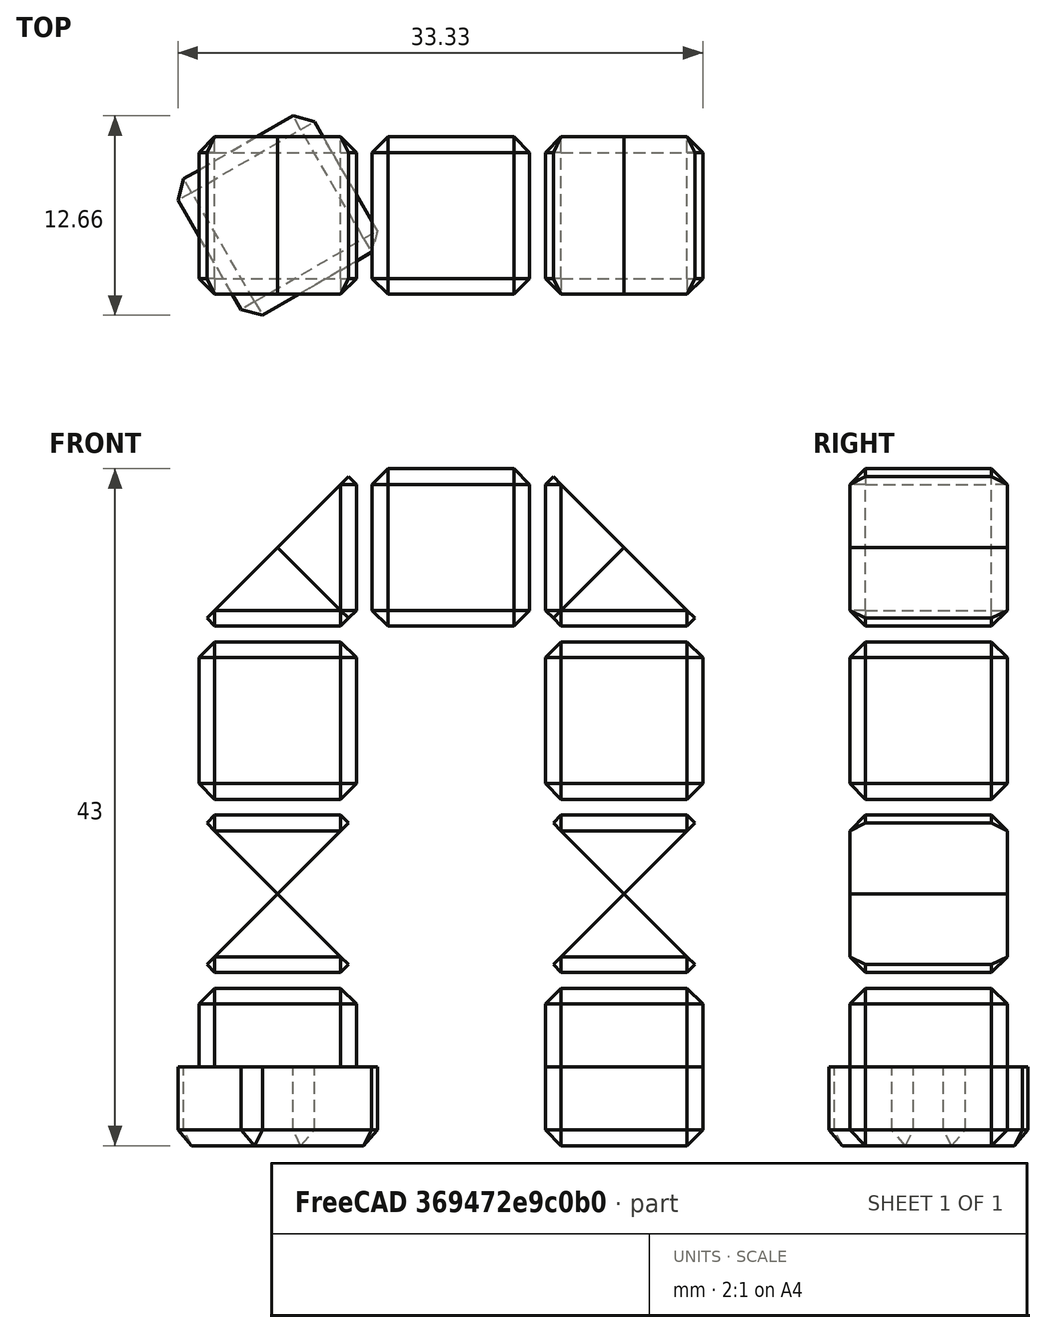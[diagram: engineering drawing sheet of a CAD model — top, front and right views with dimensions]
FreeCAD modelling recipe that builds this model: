
FCSTD DOCUMENT  (FreeCAD 0.18.4R)
Label: robot-layout
License: All rights reserved
LicenseURL: http://en.wikipedia.org/wiki/All_rights_reserved
objects: Part::Box×43, Part::Chamfer×15, Part::Cut×14, Part::Mirroring×9, Part::Fuse×8, Part::MultiCommon×6
note: 95 computed .brp shape members not serialized (recipe doc carries the construction recipe); baked Part::Feature solids carry a one-line shape summary decoded from their .brp

FEATURE [Part::Box] Box  label="Cube"
  AttacherType = Attacher::AttachEngine3D
  Height = 10
  Length = 10
  Width = 10
FEATURE [Part::Chamfer] Chamfer
  Base = -> Box
  Edges = 12 edges r=1: [Edge1,Edge2,Edge3,Edge4,Edge5,Edge6,Edge7,Edge8,Edge9,Edge10,Edge11,Edge12]
FEATURE [Part::Box] Box001  label="Cube001"
  AttacherType = Attacher::AttachEngine3D
  Height = 10
  Length = 10
  Width = 10
FEATURE [Part::Chamfer] Chamfer001
  Base = -> Box001
  Edges = 12 edges r=1: [Edge1,Edge2,Edge3,Edge4,Edge5,Edge6,Edge7,Edge8,Edge9,Edge10,Edge11,Edge12]
  Placement = pos=(0,0,11) rot=(0,0,1;0rad)
FEATURE [Part::Box] Box002  label="Cube002"
  AttacherType = Attacher::AttachEngine3D
  Height = 10
  Length = 10
  Width = 10
FEATURE [Part::Chamfer] Chamfer002
  Base = -> Box002
  Edges = 12 edges r=1: [Edge1,Edge2,Edge3,Edge4,Edge5,Edge6,Edge7,Edge8,Edge9,Edge10,Edge11,Edge12]
  Placement = pos=(0,0,22) rot=(0,0,1;0rad)
FEATURE [Part::Box] Box004  label="Cube004"
  AttacherType = Attacher::AttachEngine3D
  Height = 10
  Length = 10
  Width = 10
FEATURE [Part::Chamfer] Chamfer004
  Base = -> Box004
  Edges = 12 edges r=1: [Edge1,Edge2,Edge3,Edge4,Edge5,Edge6,Edge7,Edge8,Edge9,Edge10,Edge11,Edge12]
  Placement = pos=(11,0,33) rot=(0,0,1;0rad)
FEATURE [Part::Box] Box006  label="Cube006"
  AttacherType = Attacher::AttachEngine3D
  Height = 10
  Length = 10
  Width = 10
FEATURE [Part::Chamfer] Chamfer006
  Base = -> Box006
  Edges = 12 edges r=1: [Edge1,Edge2,Edge3,Edge4,Edge5,Edge6,Edge7,Edge8,Edge9,Edge10,Edge11,Edge12]
  Placement = pos=(22,0,22) rot=(0,0,1;0rad)
FEATURE [Part::Box] Box009  label="Cube009"
  AttacherType = Attacher::AttachEngine3D
  Height = 10
  Length = 15
  Placement = pos=(-2,-2,-5) rot=(0,0,1;0rad)
  Width = 16
FEATURE [Part::Box] Box010  label="Cube010"
  AttacherType = Attacher::AttachEngine3D
  Height = 10
  Length = 10
  Width = 10
FEATURE [Part::Chamfer] Chamfer009
  Base = -> Box010
  Edges = 12 edges r=1: [Edge1,Edge2,Edge3,Edge4,Edge5,Edge6,Edge7,Edge8,Edge9,Edge10,Edge11,Edge12]
FEATURE [Part::Box] Box011  label="Cube011"
  AttacherType = Attacher::AttachEngine3D
  Height = 10
  Length = 15
  Placement = pos=(-2,-2,-5) rot=(0,0,1;0rad)
  Width = 16
FEATURE [Part::MultiCommon] Common
  Placement = pos=(3.16987,-1.83013,0) rot=(0,0,1;0.523599rad)
  Shapes = -> [Box011,Chamfer009]
FEATURE [Part::Cut] Cut
  Base = -> Chamfer
  Tool = -> Box009
FEATURE [Part::Box] Box012  label="Cube012"
  AttacherType = Attacher::AttachEngine3D
  Height = 10
  Length = 10
  Width = 10
FEATURE [Part::Chamfer] Chamfer010
  Base = -> Box012
  Edges = 12 edges r=1: [Edge1,Edge2,Edge3,Edge4,Edge5,Edge6,Edge7,Edge8,Edge9,Edge10,Edge11,Edge12]
FEATURE [Part::Box] Box013  label="Cube013"
  AttacherType = Attacher::AttachEngine3D
  Height = 10
  Length = 15
  Placement = pos=(-2,-2,-5) rot=(0,0,1;0rad)
  Width = 16
FEATURE [Part::Box] Box014  label="Cube014"
  AttacherType = Attacher::AttachEngine3D
  Height = 10
  Length = 15
  Placement = pos=(-2,-2,-5) rot=(0,0,1;0rad)
  Width = 16
FEATURE [Part::Box] Box015  label="Cube015"
  AttacherType = Attacher::AttachEngine3D
  Height = 10
  Length = 10
  Width = 10
FEATURE [Part::Chamfer] Chamfer011
  Base = -> Box015
  Edges = 12 edges r=1: [Edge1,Edge2,Edge3,Edge4,Edge5,Edge6,Edge7,Edge8,Edge9,Edge10,Edge11,Edge12]
FEATURE [Part::MultiCommon] Common001
  Placement = pos=(22,0,0) rot=(0,0,1;0rad)
  Shapes = -> [Box014,Chamfer011]
FEATURE [Part::Cut] Cut001
  Base = -> Chamfer010
  Placement = pos=(22,0,0) rot=(0,0,1;0rad)
  Tool = -> Box013
FEATURE [Part::Box] Box016  label="Cube016"
  AttacherType = Attacher::AttachEngine3D
  Height = 10
  Length = 10
  Placement = pos=(5,-5,16) rot=(0,1,0;0.785398rad)
  Width = 21
FEATURE [Part::Box] Box017  label="Cube017"
  AttacherType = Attacher::AttachEngine3D
  Height = 10
  Length = 10
  Placement = pos=(5,-5,16) rot=(0,1,0;0.785398rad)
  Width = 21
FEATURE [Part::Mirroring] Part__Mirroring  label="Cube017 (Mirror #1)"
  Base = (0,0,0)
  Normal = (1,0,0)
  Placement = pos=(10,0,0) rot=(0,0,1;0rad)
  Source = -> Box017
FEATURE [Part::Fuse] Fusion
  Base = -> Box016
  Tool = -> Part__Mirroring
FEATURE [Part::Box] Box019  label="Cube019"
  AttacherType = Attacher::AttachEngine3D
  Height = 10
  Length = 10
  Placement = pos=(5,-5,16) rot=(0,1,0;0.785398rad)
  Width = 21
FEATURE [Part::Box] Box020  label="Cube020"
  AttacherType = Attacher::AttachEngine3D
  Height = 10
  Length = 10
  Placement = pos=(5,-5,16) rot=(0,1,0;0.785398rad)
  Width = 21
FEATURE [Part::Mirroring] Part__Mirroring001  label="Cube017 (Mirror #1)001"
  Base = (0,0,0)
  Normal = (1,0,0)
  Placement = pos=(10,0,0) rot=(0,0,1;0rad)
  Source = -> Box020
FEATURE [Part::Fuse] Fusion001
  Base = -> Box019
  Tool = -> Part__Mirroring001
FEATURE [Part::Box] Box021  label="Cube021"
  AttacherType = Attacher::AttachEngine3D
  Height = 10
  Length = 10
  Width = 10
FEATURE [Part::Chamfer] Chamfer012
  Base = -> Box021
  Edges = 12 edges r=1: [Edge1,Edge2,Edge3,Edge4,Edge5,Edge6,Edge7,Edge8,Edge9,Edge10,Edge11,Edge12]
  Placement = pos=(0,0,11) rot=(0,0,1;0rad)
FEATURE [Part::Box] Box022  label="Cube022"
  AttacherType = Attacher::AttachEngine3D
  Height = 10
  Length = 15
  Placement = pos=(-2,-2,6) rot=(0,0,1;0rad)
  Width = 16
FEATURE [Part::Box] Box023  label="Cube023"
  AttacherType = Attacher::AttachEngine3D
  Height = 10
  Length = 15
  Placement = pos=(-2,-2,6) rot=(0,0,1;0rad)
  Width = 16
FEATURE [Part::Cut] Cut002
  Base = -> Chamfer001
  Tool = -> Box022
FEATURE [Part::MultiCommon] Common002
  Shapes = -> [Box023,Chamfer012]
FEATURE [Part::Cut] Cut003
  Base = -> Cut002
  Tool = -> Fusion001
FEATURE [Part::Cut] Cut004
  Base = -> Common002
  Tool = -> Fusion
FEATURE [Part::Box] Box024  label="Cube024"
  AttacherType = Attacher::AttachEngine3D
  Height = 10
  Length = 10
  Width = 10
FEATURE [Part::Chamfer] Chamfer013
  Base = -> Box024
  Edges = 12 edges r=1: [Edge1,Edge2,Edge3,Edge4,Edge5,Edge6,Edge7,Edge8,Edge9,Edge10,Edge11,Edge12]
  Placement = pos=(0,0,11) rot=(0,0,1;0rad)
FEATURE [Part::Box] Box025  label="Cube025"
  AttacherType = Attacher::AttachEngine3D
  Height = 10
  Length = 10
  Placement = pos=(5,-5,16) rot=(0,1,0;0.785398rad)
  Width = 21
FEATURE [Part::Box] Box026  label="Cube026"
  AttacherType = Attacher::AttachEngine3D
  Height = 10
  Length = 10
  Placement = pos=(5,-5,16) rot=(0,1,0;0.785398rad)
  Width = 21
FEATURE [Part::Mirroring] Part__Mirroring002  label="Cube017 (Mirror #1)002"
  Base = (0,0,0)
  Normal = (1,0,0)
  Placement = pos=(10,0,0) rot=(0,0,1;0rad)
  Source = -> Box026
FEATURE [Part::Fuse] Fusion002
  Base = -> Box025
  Tool = -> Part__Mirroring002
FEATURE [Part::Box] Box027  label="Cube027"
  AttacherType = Attacher::AttachEngine3D
  Height = 10
  Length = 15
  Placement = pos=(-2,-2,6) rot=(0,0,1;0rad)
  Width = 16
FEATURE [Part::Cut] Cut005
  Base = -> Chamfer013
  Tool = -> Box027
FEATURE [Part::Cut] Cut006
  Base = -> Cut005
  Placement = pos=(-11,0,43) rot=(0,1,0;1.5708rad)
  Tool = -> Fusion002
FEATURE [Part::Box] Box028  label="Cube028"
  AttacherType = Attacher::AttachEngine3D
  Height = 10
  Length = 10
  Placement = pos=(5,-5,16) rot=(0,1,0;0.785398rad)
  Width = 21
FEATURE [Part::Box] Box029  label="Cube029"
  AttacherType = Attacher::AttachEngine3D
  Height = 10
  Length = 10
  Placement = pos=(5,-5,16) rot=(0,1,0;0.785398rad)
  Width = 21
FEATURE [Part::Mirroring] Part__Mirroring003  label="Cube017 (Mirror #1)003"
  Base = (0,0,0)
  Normal = (1,0,0)
  Placement = pos=(10,0,0) rot=(0,0,1;0rad)
  Source = -> Box029
FEATURE [Part::Fuse] Fusion003
  Base = -> Box028
  Tool = -> Part__Mirroring003
FEATURE [Part::Box] Box030  label="Cube030"
  AttacherType = Attacher::AttachEngine3D
  Height = 10
  Length = 10
  Width = 10
FEATURE [Part::Chamfer] Chamfer014
  Base = -> Box030
  Edges = 12 edges r=1: [Edge1,Edge2,Edge3,Edge4,Edge5,Edge6,Edge7,Edge8,Edge9,Edge10,Edge11,Edge12]
  Placement = pos=(0,0,11) rot=(0,0,1;0rad)
FEATURE [Part::Box] Box031  label="Cube031"
  AttacherType = Attacher::AttachEngine3D
  Height = 10
  Length = 15
  Placement = pos=(-2,-2,6) rot=(0,0,1;0rad)
  Width = 16
FEATURE [Part::MultiCommon] Common003
  Shapes = -> [Box031,Chamfer014]
FEATURE [Part::Cut] Cut007
  Base = -> Common003
  Placement = pos=(0,0,22) rot=(0,0,1;0rad)
  Tool = -> Fusion003
FEATURE [Part::Box] Box032  label="Cube032"
  AttacherType = Attacher::AttachEngine3D
  Height = 10
  Length = 10
  Placement = pos=(5,-5,16) rot=(0,1,0;0.785398rad)
  Width = 21
FEATURE [Part::Box] Box033  label="Cube033"
  AttacherType = Attacher::AttachEngine3D
  Height = 10
  Length = 10
  Width = 10
FEATURE [Part::Box] Box034  label="Cube034"
  AttacherType = Attacher::AttachEngine3D
  Height = 10
  Length = 10
  Placement = pos=(5,-5,16) rot=(0,1,0;0.785398rad)
  Width = 21
FEATURE [Part::Chamfer] Chamfer015
  Base = -> Box033
  Edges = 12 edges r=1: [Edge1,Edge2,Edge3,Edge4,Edge5,Edge6,Edge7,Edge8,Edge9,Edge10,Edge11,Edge12]
  Placement = pos=(0,0,11) rot=(0,0,1;0rad)
FEATURE [Part::Mirroring] Part__Mirroring004  label="Cube017 (Mirror #1)004"
  Base = (0,0,0)
  Normal = (1,0,0)
  Placement = pos=(10,0,0) rot=(0,0,1;0rad)
  Source = -> Box034
FEATURE [Part::Fuse] Fusion004
  Base = -> Box032
  Tool = -> Part__Mirroring004
FEATURE [Part::Box] Box035  label="Cube035"
  AttacherType = Attacher::AttachEngine3D
  Height = 10
  Length = 15
  Placement = pos=(-2,-2,6) rot=(0,0,1;0rad)
  Width = 16
FEATURE [Part::Cut] Cut009
  Base = -> Chamfer015
  Tool = -> Box035
FEATURE [Part::Cut] Cut008
  Base = -> Cut009
  Placement = pos=(-11,0,43) rot=(0,1,0;1.5708rad)
  Tool = -> Fusion004
FEATURE [Part::Mirroring] Part__Mirroring005  label="Cut008 (Mirror #6)"
  Base = (-5,0,0)
  Normal = (1,0,0)
  Placement = pos=(42,0,0) rot=(0,0,1;0rad)
  Source = -> Cut008
FEATURE [Part::Box] Box036  label="Cube036"
  AttacherType = Attacher::AttachEngine3D
  Height = 10
  Length = 10
  Placement = pos=(5,-5,16) rot=(0,1,0;0.785398rad)
  Width = 21
FEATURE [Part::Box] Box037  label="Cube037"
  AttacherType = Attacher::AttachEngine3D
  Height = 10
  Length = 15
  Placement = pos=(-2,-2,6) rot=(0,0,1;0rad)
  Width = 16
FEATURE [Part::Box] Box038  label="Cube038"
  AttacherType = Attacher::AttachEngine3D
  Height = 10
  Length = 10
  Placement = pos=(5,-5,16) rot=(0,1,0;0.785398rad)
  Width = 21
FEATURE [Part::Mirroring] Part__Mirroring006  label="Cube017 (Mirror #1)005"
  Base = (0,0,0)
  Normal = (1,0,0)
  Placement = pos=(10,0,0) rot=(0,0,1;0rad)
  Source = -> Box038
FEATURE [Part::Box] Box039  label="Cube039"
  AttacherType = Attacher::AttachEngine3D
  Height = 10
  Length = 10
  Width = 10
FEATURE [Part::Chamfer] Chamfer016
  Base = -> Box039
  Edges = 12 edges r=1: [Edge1,Edge2,Edge3,Edge4,Edge5,Edge6,Edge7,Edge8,Edge9,Edge10,Edge11,Edge12]
  Placement = pos=(0,0,11) rot=(0,0,1;0rad)
FEATURE [Part::MultiCommon] Common004
  Shapes = -> [Box037,Chamfer016]
FEATURE [Part::Fuse] Fusion005
  Base = -> Box036
  Tool = -> Part__Mirroring006
FEATURE [Part::Cut] Cut010
  Base = -> Common004
  Placement = pos=(22,0,22) rot=(0,0,1;0rad)
  Tool = -> Fusion005
FEATURE [Part::Box] Box040  label="Cube040"
  AttacherType = Attacher::AttachEngine3D
  Height = 10
  Length = 10
  Width = 10
FEATURE [Part::Chamfer] Chamfer017
  Base = -> Box040
  Edges = 12 edges r=1: [Edge1,Edge2,Edge3,Edge4,Edge5,Edge6,Edge7,Edge8,Edge9,Edge10,Edge11,Edge12]
  Placement = pos=(0,0,11) rot=(0,0,1;0rad)
FEATURE [Part::Box] Box041  label="Cube041"
  AttacherType = Attacher::AttachEngine3D
  Height = 10
  Length = 10
  Placement = pos=(5,-5,16) rot=(0,1,0;0.785398rad)
  Width = 21
FEATURE [Part::Box] Box042  label="Cube042"
  AttacherType = Attacher::AttachEngine3D
  Height = 10
  Length = 10
  Placement = pos=(5,-5,16) rot=(0,1,0;0.785398rad)
  Width = 21
FEATURE [Part::Mirroring] Part__Mirroring007  label="Cube017 (Mirror #1)006"
  Base = (0,0,0)
  Normal = (1,0,0)
  Placement = pos=(10,0,0) rot=(0,0,1;0rad)
  Source = -> Box042
FEATURE [Part::Fuse] Fusion006
  Base = -> Box041
  Tool = -> Part__Mirroring007
FEATURE [Part::Box] Box043  label="Cube043"
  AttacherType = Attacher::AttachEngine3D
  Height = 10
  Length = 15
  Placement = pos=(-2,-2,6) rot=(0,0,1;0rad)
  Width = 16
FEATURE [Part::Cut] Cut011
  Base = -> Chamfer017
  Tool = -> Box043
FEATURE [Part::Cut] Cut012
  Base = -> Cut011
  Placement = pos=(22,0,0) rot=(0,0,1;0rad)
  Tool = -> Fusion006
FEATURE [Part::Box] Box044  label="Cube044"
  AttacherType = Attacher::AttachEngine3D
  Height = 10
  Length = 10
  Placement = pos=(5,-5,16) rot=(0,1,0;0.785398rad)
  Width = 21
FEATURE [Part::Box] Box045  label="Cube045"
  AttacherType = Attacher::AttachEngine3D
  Height = 10
  Length = 10
  Placement = pos=(5,-5,16) rot=(0,1,0;0.785398rad)
  Width = 21
FEATURE [Part::Mirroring] Part__Mirroring008  label="Cube017 (Mirror #1)007"
  Base = (0,0,0)
  Normal = (1,0,0)
  Placement = pos=(10,0,0) rot=(0,0,1;0rad)
  Source = -> Box045
FEATURE [Part::Fuse] Fusion007
  Base = -> Box044
  Tool = -> Part__Mirroring008
FEATURE [Part::Box] Box046  label="Cube046"
  AttacherType = Attacher::AttachEngine3D
  Height = 10
  Length = 10
  Width = 10
FEATURE [Part::Chamfer] Chamfer018
  Base = -> Box046
  Edges = 12 edges r=1: [Edge1,Edge2,Edge3,Edge4,Edge5,Edge6,Edge7,Edge8,Edge9,Edge10,Edge11,Edge12]
  Placement = pos=(0,0,11) rot=(0,0,1;0rad)
FEATURE [Part::Box] Box047  label="Cube047"
  AttacherType = Attacher::AttachEngine3D
  Height = 10
  Length = 15
  Placement = pos=(-2,-2,6) rot=(0,0,1;0rad)
  Width = 16
FEATURE [Part::MultiCommon] Common005
  Shapes = -> [Box047,Chamfer018]
FEATURE [Part::Cut] Cut013
  Base = -> Common005
  Placement = pos=(22,0,0) rot=(0,0,1;0rad)
  Tool = -> Fusion007
